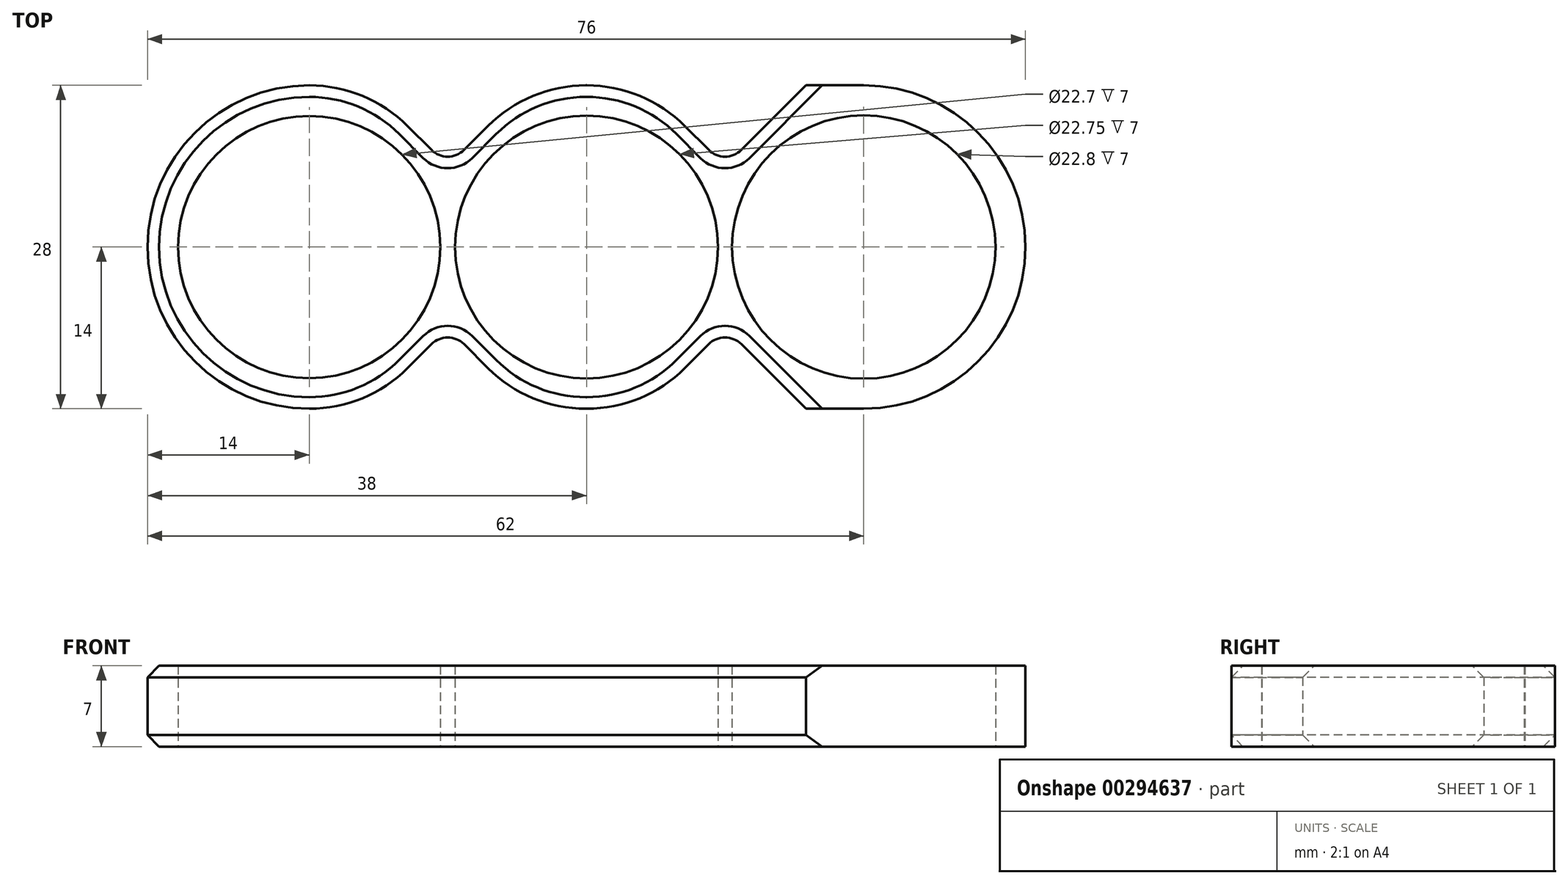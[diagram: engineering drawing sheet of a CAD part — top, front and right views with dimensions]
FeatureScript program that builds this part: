
annotation { "Feature Type Name" : "Feature", "Feature Type Description" : "" }
export const myFeature = defineFeature(function(context is Context, id is Id, definition is map)
    precondition{}
    {
        {
            var Q0;
            Q0=qCreatedBy(makeId("Top.planeOp"),FACE);
            var sketch = newSketch(context, id + "F0", { "sketchPlane" : qUnion([Q0])});
            skLineSegment(sketch, "E0.bottom", {"start": v(38, 14) * mm, "end": v(-38, 14) * mm});
            skLineSegment(sketch, "E0.top", {"start": v(38, -14) * mm, "end": v(-38, -14) * mm});
            skLineSegment(sketch, "E0.left", {"start": v(38, 14) * mm, "end": v(38, -14) * mm});
            skLineSegment(sketch, "E0.right", {"start": v(-38, 14) * mm, "end": v(-38, -14) * mm});
            skPoint(sketch, "E0.middle", {"position": v(0, 0) * mm});
            skCircle(sketch, "E1", {"center": v(0, 0) * mm, "radius": 11.38 * mm});
            skCircle(sketch, "E2", {"center": v(-24, 0) * mm, "radius": 11.35 * mm});
            skCircle(sketch, "E3", {"center": v(24, 0) * mm, "radius": 11.4 * mm});
            skSolve(sketch);
        }
        {
            var Q0;
            Q0=makeQuery(id+"F0.imprint","IMPRINT",FACE,{"disambiguationData":[TD([[makeQuery(id+"F0.imprint","IMPRINT",EDGE,{"derivedFrom":sQuery(id+"F0.wireOp",EDGE,"E0.bottom")}),1.0]])]});
            extrude(context, id + "F1", {"entities" : qUnion([Q0]), "depth" : 7 * mm});
        }
        {
            var Q0;
            Q0=makeQuery(id+"F1.opExtrude","CAP_FACE",FACE,{"disambiguationData":[OSD([sQuery(id+"F0.wireOp",EDGE,"E0.bottom"),sQuery(id+"F0.wireOp",EDGE,"E0.top"),sQuery(id+"F0.wireOp",EDGE,"E0.left"),sQuery(id+"F0.wireOp",EDGE,"E0.right"),sQuery(id+"F0.wireOp",EDGE,"E1"),sQuery(id+"F0.wireOp",EDGE,"E2"),sQuery(id+"F0.wireOp",EDGE,"E3")])],"isStart":false});
            var sketch = newSketch(context, id + "F2", { "sketchPlane" : qUnion([Q0])});
            skLineSegment(sketch, "E4", {"start": v(-19.01, 14) * mm, "end": v(-12.01, 7) * mm});
            skLineSegment(sketch, "E5", {"start": v(-12.01, 7) * mm, "end": v(-5.01, 14) * mm});
            skLineSegment(sketch, "E6", {"start": v(-5.01, 14) * mm, "end": v(-19.01, 14) * mm});
            skLineSegment(sketch, "E7", {"start": v(-19.01, -14) * mm, "end": v(-12.01, -7) * mm});
            skLineSegment(sketch, "E8", {"start": v(-12.01, -7) * mm, "end": v(-5.01, -14) * mm});
            skLineSegment(sketch, "E9", {"start": v(-5.01, -14) * mm, "end": v(-19.01, -14) * mm});
            skLineSegment(sketch, "E10", {"start": v(4.99, 14) * mm, "end": v(11.99, 7) * mm});
            skLineSegment(sketch, "E11", {"start": v(11.99, 7) * mm, "end": v(18.99, 14) * mm});
            skLineSegment(sketch, "E12", {"start": v(18.99, 14) * mm, "end": v(4.99, 14) * mm});
            skLineSegment(sketch, "E13", {"start": v(4.99, -14) * mm, "end": v(11.99, -7) * mm});
            skLineSegment(sketch, "E14", {"start": v(11.99, -7) * mm, "end": v(18.99, -14) * mm});
            skLineSegment(sketch, "E15", {"start": v(18.99, -14) * mm, "end": v(4.99, -14) * mm});
            skLineSegment(sketch, "E16", {"start": v(11.38, 0) * mm, "end": v(12.6, 0) * mm});
            skLineSegment(sketch, "E17", {"start": v(11.99, 7) * mm, "end": v(11.99, 0) * mm});
            skLineSegment(sketch, "E18", {"start": v(11.99, 0) * mm, "end": v(11.99, -7) * mm});
            skLineSegment(sketch, "E19", {"start": v(-12.65, 0) * mm, "end": v(-11.38, 0) * mm});
            skLineSegment(sketch, "E20", {"start": v(-12.01, 7) * mm, "end": v(-12.01, 0) * mm});
            skLineSegment(sketch, "E21", {"start": v(-12.01, 0) * mm, "end": v(-12.01, -7) * mm});
            skSolve(sketch);
        }
        {
            var Q0;
            Q0=makeQuery(id+"F2.imprint","IMPRINT",FACE,{"disambiguationData":[TD([[makeQuery(id+"F2.imprint","IMPRINT",EDGE,{"derivedFrom":sQuery(id+"F2.wireOp",EDGE,"E4")}),1.0]])]});
            var Q1;
            Q1=makeQuery(id+"F2.imprint","IMPRINT",FACE,{"disambiguationData":[TD([[makeQuery(id+"F2.imprint","IMPRINT",EDGE,{"derivedFrom":sQuery(id+"F2.wireOp",EDGE,"E10")}),1.0]])]});
            var Q2;
            Q2=makeQuery(id+"F2.imprint","IMPRINT",FACE,{"disambiguationData":[TD([[makeQuery(id+"F2.imprint","IMPRINT",EDGE,{"derivedFrom":sQuery(id+"F2.wireOp",EDGE,"E13")}),-1.0]])]});
            var Q3;
            Q3=makeQuery(id+"F2.imprint","IMPRINT",FACE,{"disambiguationData":[TD([[makeQuery(id+"F2.imprint","IMPRINT",EDGE,{"derivedFrom":sQuery(id+"F2.wireOp",EDGE,"E7")}),-1.0]])]});
            extrude(context, id + "F3", {"entities" : qUnion([Q0, Q1, Q2, Q3]), "operationType" : NewBodyOperationType.REMOVE, "endBound" : BoundingType.THROUGH_ALL, "oppositeDirection" : true, "depth" : 25 * mm});
        }
        {
            var Q0;
            Q0=makeQuery(id+"F1.opExtrude","SWEPT_EDGE",EDGE,{"disambiguationData":[OSD([sQuery(id+"F0.wireOp",EDGE,"E0.top"),sQuery(id+"F0.wireOp",EDGE,"E0.right")])]});
            var Q1;
            Q1=makeQuery(id+"F1.opExtrude","SWEPT_EDGE",EDGE,{"disambiguationData":[OSD([sQuery(id+"F0.wireOp",EDGE,"E0.bottom"),sQuery(id+"F0.wireOp",EDGE,"E0.right")])]});
            var Q2;
            Q2=makeQuery(id+"F1.opExtrude","SWEPT_EDGE",EDGE,{"disambiguationData":[OSD([sQuery(id+"F0.wireOp",EDGE,"E0.top"),sQuery(id+"F0.wireOp",EDGE,"E0.left")])]});
            var Q3;
            Q3=makeQuery(id+"F1.opExtrude","SWEPT_EDGE",EDGE,{"disambiguationData":[OSD([sQuery(id+"F0.wireOp",EDGE,"E0.bottom"),sQuery(id+"F0.wireOp",EDGE,"E0.left")])]});
            fillet(context, id + "F4", {"entities" : qUnion([Q0, Q1, Q2, Q3]), "radius" : 14 * mm, "tangentPropagation" : true, "allowEdgeOverflow" : false});
        }
        {
            var Q0;
            Q0=makeQuery(id+"F3.boolean.opBoolean","COPY",EDGE,{"derivedFrom":makeQuery(id+"F3.opExtrude","SWEPT_EDGE",EDGE,{"disambiguationData":[OSD([sQuery(id+"F0.wireOp",EDGE,"E0.top"),sQuery(id+"F2.wireOp",EDGE,"E7"),sQuery(id+"F2.wireOp",EDGE,"E9")])]})});
            var Q1;
            Q1=makeQuery(id+"F3.boolean.opBoolean","COPY",EDGE,{"derivedFrom":makeQuery(id+"F3.opExtrude","SWEPT_EDGE",EDGE,{"disambiguationData":[OSD([sQuery(id+"F0.wireOp",EDGE,"E0.top"),sQuery(id+"F2.wireOp",EDGE,"E8"),sQuery(id+"F2.wireOp",EDGE,"E9")])]})});
            var Q2;
            Q2=makeQuery(id+"F3.boolean.opBoolean","COPY",EDGE,{"derivedFrom":makeQuery(id+"F3.opExtrude","SWEPT_EDGE",EDGE,{"disambiguationData":[OSD([sQuery(id+"F0.wireOp",EDGE,"E0.top"),sQuery(id+"F2.wireOp",EDGE,"E13"),sQuery(id+"F2.wireOp",EDGE,"E15")])]})});
            var Q3;
            Q3=makeQuery(id+"F3.boolean.opBoolean","COPY",EDGE,{"derivedFrom":makeQuery(id+"F3.opExtrude","SWEPT_EDGE",EDGE,{"disambiguationData":[OSD([sQuery(id+"F0.wireOp",EDGE,"E0.top"),sQuery(id+"F2.wireOp",EDGE,"E14"),sQuery(id+"F2.wireOp",EDGE,"E15")])]})});
            var Q4;
            Q4=makeQuery(id+"F3.boolean.opBoolean","COPY",EDGE,{"derivedFrom":makeQuery(id+"F3.opExtrude","SWEPT_EDGE",EDGE,{"disambiguationData":[OSD([sQuery(id+"F0.wireOp",EDGE,"E0.bottom"),sQuery(id+"F2.wireOp",EDGE,"E11"),sQuery(id+"F2.wireOp",EDGE,"E12")])]})});
            var Q5;
            Q5=makeQuery(id+"F3.boolean.opBoolean","COPY",EDGE,{"derivedFrom":makeQuery(id+"F3.opExtrude","SWEPT_EDGE",EDGE,{"disambiguationData":[OSD([sQuery(id+"F0.wireOp",EDGE,"E0.bottom"),sQuery(id+"F2.wireOp",EDGE,"E10"),sQuery(id+"F2.wireOp",EDGE,"E12")])]})});
            var Q6;
            Q6=makeQuery(id+"F3.boolean.opBoolean","COPY",EDGE,{"derivedFrom":makeQuery(id+"F3.opExtrude","SWEPT_EDGE",EDGE,{"disambiguationData":[OSD([sQuery(id+"F0.wireOp",EDGE,"E0.bottom"),sQuery(id+"F2.wireOp",EDGE,"E5"),sQuery(id+"F2.wireOp",EDGE,"E6")])]})});
            var Q7;
            Q7=makeQuery(id+"F3.boolean.opBoolean","COPY",EDGE,{"derivedFrom":makeQuery(id+"F3.opExtrude","SWEPT_EDGE",EDGE,{"disambiguationData":[OSD([sQuery(id+"F0.wireOp",EDGE,"E0.bottom"),sQuery(id+"F2.wireOp",EDGE,"E4"),sQuery(id+"F2.wireOp",EDGE,"E6")])]})});
            fillet(context, id + "F5", {"entities" : qUnion([Q0, Q1, Q2, Q3, Q4, Q5, Q6, Q7]), "radius" : 12 * mm, "tangentPropagation" : true, "allowEdgeOverflow" : false});
        }
        {
            var Q0;
            Q0=makeQuery(id+"F3.boolean.opBoolean","COPY",EDGE,{"derivedFrom":makeQuery(id+"F3.opExtrude","SWEPT_EDGE",EDGE,{"disambiguationData":[OSD([sQuery(id+"F2.wireOp",EDGE,"E7"),sQuery(id+"F2.wireOp",EDGE,"E8"),sQuery(id+"F2.wireOp",EDGE,"E21")])]})});
            var Q1;
            Q1=makeQuery(id+"F3.boolean.opBoolean","COPY",EDGE,{"derivedFrom":makeQuery(id+"F3.opExtrude","SWEPT_EDGE",EDGE,{"disambiguationData":[OSD([sQuery(id+"F2.wireOp",EDGE,"E13"),sQuery(id+"F2.wireOp",EDGE,"E14"),sQuery(id+"F2.wireOp",EDGE,"E18")])]})});
            var Q2;
            Q2=makeQuery(id+"F3.boolean.opBoolean","COPY",EDGE,{"derivedFrom":makeQuery(id+"F3.opExtrude","SWEPT_EDGE",EDGE,{"disambiguationData":[OSD([sQuery(id+"F2.wireOp",EDGE,"E4"),sQuery(id+"F2.wireOp",EDGE,"E5"),sQuery(id+"F2.wireOp",EDGE,"E20")])]})});
            var Q3;
            Q3=makeQuery(id+"F3.boolean.opBoolean","COPY",EDGE,{"derivedFrom":makeQuery(id+"F3.opExtrude","SWEPT_EDGE",EDGE,{"disambiguationData":[OSD([sQuery(id+"F2.wireOp",EDGE,"E10"),sQuery(id+"F2.wireOp",EDGE,"E11"),sQuery(id+"F2.wireOp",EDGE,"E17")])]})});
            fillet(context, id + "F6", {"entities" : qUnion([Q0, Q1, Q2, Q3]), "radius" : 2 * mm, "tangentPropagation" : true, "allowEdgeOverflow" : false});
        }
        {
            var Q0;
            {var subQ0=sQuery(id+"F0.wireOp",EDGE,"E0.top");Q0=makeQuery(id+"F5.opFillet","BLEND_EDGE",EDGE,{"blendedFrom":[makeQuery(id+"F3.boolean.opBoolean","COPY",EDGE,{"derivedFrom":makeQuery(id+"F3.opExtrude","SWEPT_EDGE",EDGE,{"disambiguationData":[OSD([subQ0,sQuery(id+"F2.wireOp",EDGE,"E8"),sQuery(id+"F2.wireOp",EDGE,"E9")])]})}),makeQuery(id+"F1.opExtrude","CAP_FACE",FACE,{"disambiguationData":[OSD([sQuery(id+"F0.wireOp",EDGE,"E0.bottom"),subQ0,sQuery(id+"F0.wireOp",EDGE,"E0.left"),sQuery(id+"F0.wireOp",EDGE,"E0.right"),sQuery(id+"F0.wireOp",EDGE,"E1"),sQuery(id+"F0.wireOp",EDGE,"E2"),sQuery(id+"F0.wireOp",EDGE,"E3")])],"isStart":false})],"blendedInto":[makeQuery(id+"F1.opExtrude","CAP_FACE",FACE,{"disambiguationData":[OSD([sQuery(id+"F0.wireOp",EDGE,"E0.bottom"),subQ0,sQuery(id+"F0.wireOp",EDGE,"E0.left"),sQuery(id+"F0.wireOp",EDGE,"E0.right"),sQuery(id+"F0.wireOp",EDGE,"E1"),sQuery(id+"F0.wireOp",EDGE,"E2"),sQuery(id+"F0.wireOp",EDGE,"E3")])],"isStart":false})]});}
            var Q1;
            {var subQ0=sQuery(id+"F0.wireOp",EDGE,"E0.top");Q1=makeQuery(id+"F5.opFillet","BLEND_EDGE",EDGE,{"blendedFrom":[makeQuery(id+"F3.boolean.opBoolean","COPY",EDGE,{"derivedFrom":makeQuery(id+"F3.opExtrude","SWEPT_EDGE",EDGE,{"disambiguationData":[OSD([subQ0,sQuery(id+"F2.wireOp",EDGE,"E8"),sQuery(id+"F2.wireOp",EDGE,"E9")])]})}),makeQuery(id+"F1.opExtrude","CAP_FACE",FACE,{"disambiguationData":[OSD([sQuery(id+"F0.wireOp",EDGE,"E0.bottom"),subQ0,sQuery(id+"F0.wireOp",EDGE,"E0.left"),sQuery(id+"F0.wireOp",EDGE,"E0.right"),sQuery(id+"F0.wireOp",EDGE,"E1"),sQuery(id+"F0.wireOp",EDGE,"E2"),sQuery(id+"F0.wireOp",EDGE,"E3")])],"isStart":true})],"blendedInto":[makeQuery(id+"F1.opExtrude","CAP_FACE",FACE,{"disambiguationData":[OSD([sQuery(id+"F0.wireOp",EDGE,"E0.bottom"),subQ0,sQuery(id+"F0.wireOp",EDGE,"E0.left"),sQuery(id+"F0.wireOp",EDGE,"E0.right"),sQuery(id+"F0.wireOp",EDGE,"E1"),sQuery(id+"F0.wireOp",EDGE,"E2"),sQuery(id+"F0.wireOp",EDGE,"E3")])],"isStart":true})]});}
            chamfer(context, id + "F7", {"entities" : qUnion([Q0, Q1]), "width" : 1 * mm, "tangentPropagation" : true});
        }
    });
